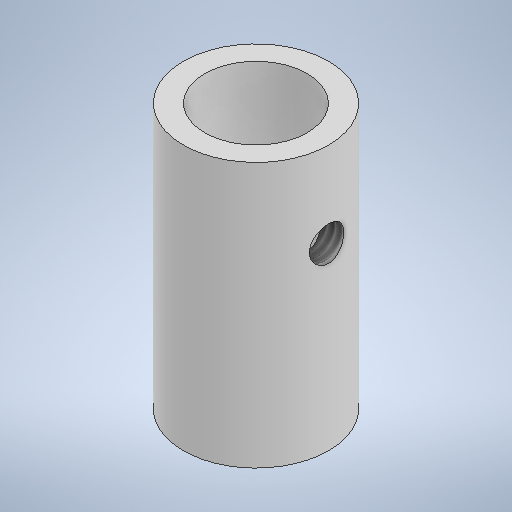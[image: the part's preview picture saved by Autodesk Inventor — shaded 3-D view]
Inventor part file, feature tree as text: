
AUTODESK INVENTOR PART (.ipt)
format: ipt  version: 2025.1 (Build 291241000, 241)  size: 239,104 bytes
history: native  units: mm
features: sketch x2, extrude x1, plane x1, hole x1
ambient origin geometry x8: Origin, YZ Plane, XZ Plane, XY Plane, X Axis, Y Axis, Z Axis, Center Point
bodies: Solid1 (feature_tree)
feature tree (5):
  extrude  "Extrusion1"  Depth=6.0mm
  plane  "Work Plane1"
  hole  "Hole1"  [1 undecoded]
  sketch  "Sketch1"  dims[d0=8.5mm d1=6.0mm]
  sketch  "Sketch2"  dims[d2=15.5mm d3=0.0mm d4=4.25mm d5=5.0mm d6=2.013mm d7=5.0mm d8=4.0mm d9=2.0mm d10=90.0deg d11=8.0mm d12=0.0mm]
note: 1 required parameter value undecoded (feature->parameter linkage not recoverable at this tier; creation-order binding heuristic only, values carry confidence <= 0.55)
